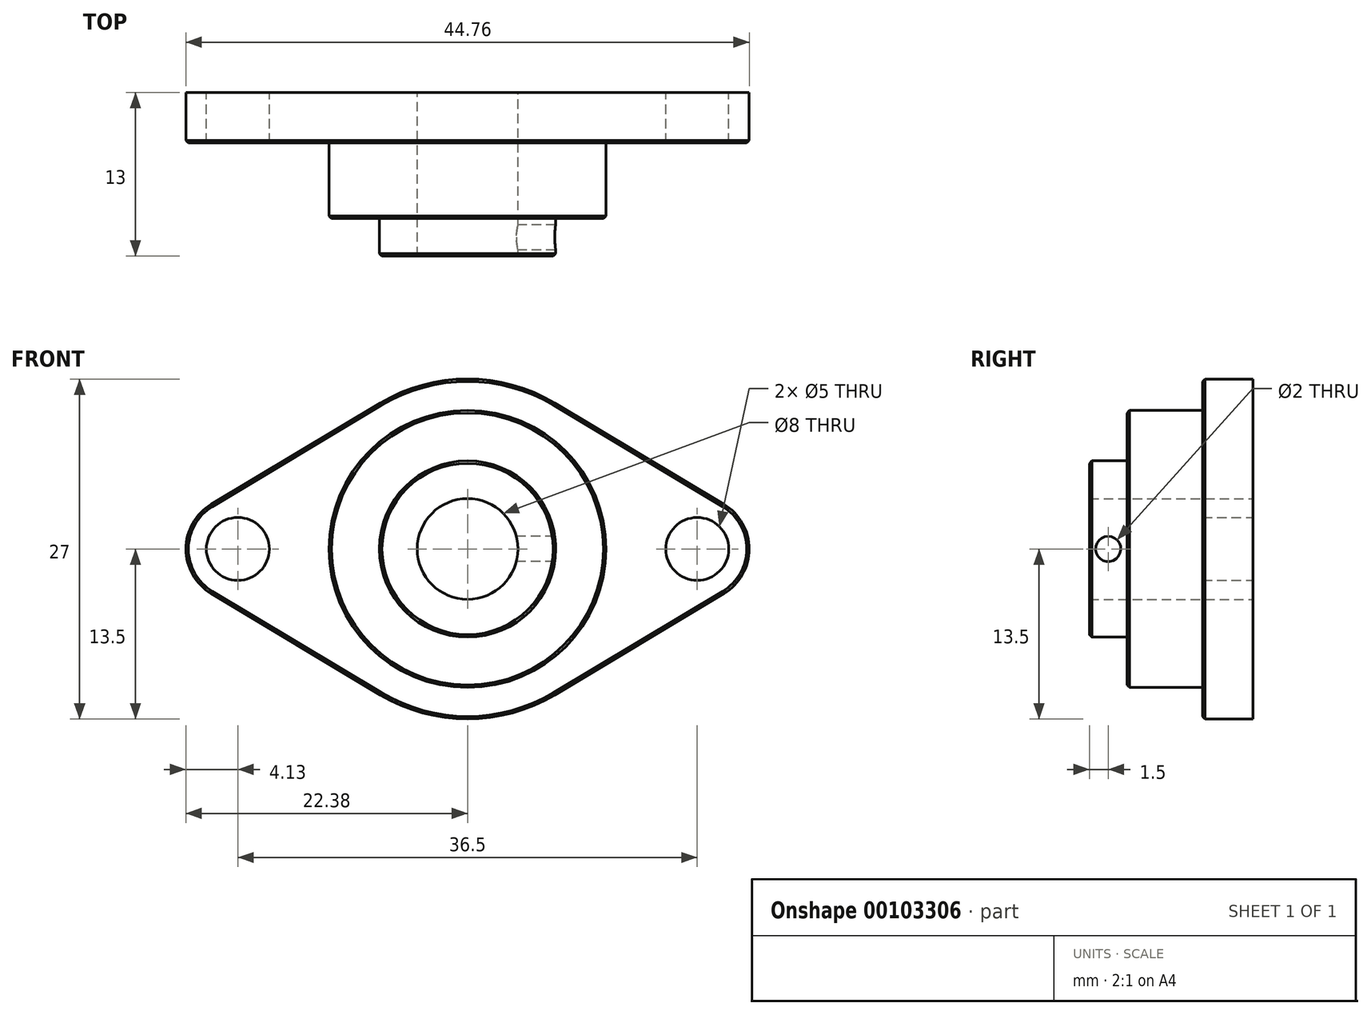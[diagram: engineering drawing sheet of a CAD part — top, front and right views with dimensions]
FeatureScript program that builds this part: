
annotation { "Feature Type Name" : "Feature", "Feature Type Description" : "" }
export const myFeature = defineFeature(function(context is Context, id is Id, definition is map)
    precondition{}
    {
        {
            var Q0;
            Q0=qCreatedBy(makeId("Front.planeOp"),FACE);
            var sketch = newSketch(context, id + "F0", { "sketchPlane" : qUnion([Q0])});
            skCircle(sketch, "E0", {"center": v(0, 0) * mm, "radius": 4 * mm});
            skArc(sketch, "E1", {"start": v(-6.93, -11.58) * mm, "mid": v(0, -13.5) * mm, "end": v(6.93, -11.58) * mm});
            skCircle(sketch, "E2", {"center": v(18.25, 0) * mm, "radius": 2.5 * mm});
            skCircle(sketch, "E3", {"center": v(-18.25, 0) * mm, "radius": 2.5 * mm});
            skArc(sketch, "E4", {"start": v(-20.37, 3.54) * mm, "mid": v(-22.38, 0) * mm, "end": v(-20.37, -3.54) * mm});
            skArc(sketch, "E5", {"start": v(20.37, -3.54) * mm, "mid": v(22.38, 0) * mm, "end": v(20.37, 3.54) * mm});
            skCircle(sketch, "E6", {"center": v(0, 0) * mm, "radius": 7 * mm});
            skCircle(sketch, "E7", {"center": v(0, 0) * mm, "radius": 11 * mm});
            skLineSegment(sketch, "E8", {"start": v(-20.37, 3.54) * mm, "end": v(-6.93, 11.58) * mm});
            skLineSegment(sketch, "E9", {"start": v(-20.37, -3.54) * mm, "end": v(-6.93, -11.58) * mm});
            skLineSegment(sketch, "E10", {"start": v(20.37, 3.54) * mm, "end": v(6.93, 11.58) * mm});
            skLineSegment(sketch, "E11", {"start": v(20.37, -3.54) * mm, "end": v(6.93, -11.58) * mm});
            skArc(sketch, "E12.trimOffspring", {"start": v(6.93, 11.58) * mm, "mid": v(0, 13.5) * mm, "end": v(-6.93, 11.58) * mm});
            skSolve(sketch);
        }
        {
            var Q0;
            Q0=makeQuery(id+"F0.imprint","IMPRINT",FACE,{"disambiguationData":[TD([[makeQuery(id+"F0.imprint","IMPRINT",EDGE,{"derivedFrom":sQuery(id+"F0.wireOp",EDGE,"E1")}),1.0]])]});
            extrude(context, id + "F1", {"entities" : qUnion([Q0]), "depth" : 4 * mm});
        }
        {
            var Q0;
            Q0=makeQuery(id+"F0.imprint","IMPRINT",FACE,{"disambiguationData":[TD([[makeQuery(id+"F0.imprint","IMPRINT",EDGE,{"derivedFrom":sQuery(id+"F0.wireOp",EDGE,"E0")}),-1.0]])]});
            extrude(context, id + "F2", {"entities" : qUnion([Q0]), "operationType" : NewBodyOperationType.ADD, "depth" : 13 * mm});
        }
        {
            var Q0;
            Q0=makeQuery(id+"F0.imprint","IMPRINT",FACE,{"disambiguationData":[TD([[makeQuery(id+"F0.imprint","IMPRINT",EDGE,{"derivedFrom":sQuery(id+"F0.wireOp",EDGE,"E6")}),-1.0]])]});
            extrude(context, id + "F3", {"entities" : qUnion([Q0]), "operationType" : NewBodyOperationType.ADD, "depth" : 10 * mm});
        }
        {
            var Q0;
            Q0=qCreatedBy(makeId("Right.planeOp"),FACE);
            var sketch = newSketch(context, id + "F4", { "sketchPlane" : qUnion([Q0])});
            skLineSegment(sketch, "E13", {"start": v(-24.08, 0) * mm, "end": v(10.78, 0) * mm, "construction": true});
            skLineSegment(sketch, "E14", {"start": v(-11.5, 15) * mm, "end": v(-11.5, -16.26) * mm, "construction": true});
            skCircle(sketch, "E15", {"center": v(-11.5, 0) * mm, "radius": 1 * mm});
            skSolve(sketch);
        }
        {
            var Q0;
            Q0=makeQuery(id+"F4.imprint","IMPRINT",FACE,{"disambiguationData":[TD([[makeQuery(id+"F4.imprint","IMPRINT",EDGE,{"derivedFrom":sQuery(id+"F4.wireOp",EDGE,"E15")}),1.0]])]});
            extrude(context, id + "F5", {"entities" : qUnion([Q0]), "operationType" : NewBodyOperationType.REMOVE, "depth" : 8 * mm});
        }
        {
            var Q0;
            Q0=makeQuery(id+"F3.opExtrude","CAP_EDGE",EDGE,{"disambiguationData":[OSD([sQuery(id+"F0.wireOp",EDGE,"E7")])],"isStart":false});
            chamfer(context, id + "F6", {"entities" : qUnion([Q0]), "width" : 0.2 * mm, "tangentPropagation" : true});
        }
        {
            var Q0;
            Q0=makeQuery(id+"F2.opExtrude","CAP_EDGE",EDGE,{"disambiguationData":[OSD([sQuery(id+"F0.wireOp",EDGE,"E6")])],"isStart":false});
            chamfer(context, id + "F7", {"entities" : qUnion([Q0]), "width" : 0.2 * mm, "tangentPropagation" : true});
        }
        {
            var Q0;
            Q0=makeQuery(id+"F1.opExtrude","CAP_EDGE",EDGE,{"disambiguationData":[OSD([sQuery(id+"F0.wireOp",EDGE,"E11")])],"isStart":false});
            var Q1;
            Q1=makeQuery(id+"F1.opExtrude","CAP_EDGE",EDGE,{"disambiguationData":[OSD([sQuery(id+"F0.wireOp",EDGE,"E10")])],"isStart":false});
            var Q2;
            Q2=makeQuery(id+"F1.opExtrude","CAP_EDGE",EDGE,{"disambiguationData":[OSD([sQuery(id+"F0.wireOp",EDGE,"E5")])],"isStart":false});
            var Q3;
            Q3=makeQuery(id+"F1.opExtrude","CAP_EDGE",EDGE,{"disambiguationData":[OSD([sQuery(id+"F0.wireOp",EDGE,"E1")])],"isStart":false});
            var Q4;
            Q4=makeQuery(id+"F1.opExtrude","CAP_EDGE",EDGE,{"disambiguationData":[OSD([sQuery(id+"F0.wireOp",EDGE,"E12.trimOffspring")])],"isStart":false});
            var Q5;
            Q5=makeQuery(id+"F1.opExtrude","CAP_EDGE",EDGE,{"disambiguationData":[OSD([sQuery(id+"F0.wireOp",EDGE,"E8")])],"isStart":false});
            var Q6;
            Q6=makeQuery(id+"F1.opExtrude","CAP_EDGE",EDGE,{"disambiguationData":[OSD([sQuery(id+"F0.wireOp",EDGE,"E9")])],"isStart":false});
            var Q7;
            Q7=makeQuery(id+"F1.opExtrude","CAP_EDGE",EDGE,{"disambiguationData":[OSD([sQuery(id+"F0.wireOp",EDGE,"E4")])],"isStart":false});
            chamfer(context, id + "F8", {"entities" : qUnion([Q0, Q1, Q2, Q3, Q4, Q5, Q6, Q7]), "width" : 0.2 * mm, "tangentPropagation" : true});
        }
    });
